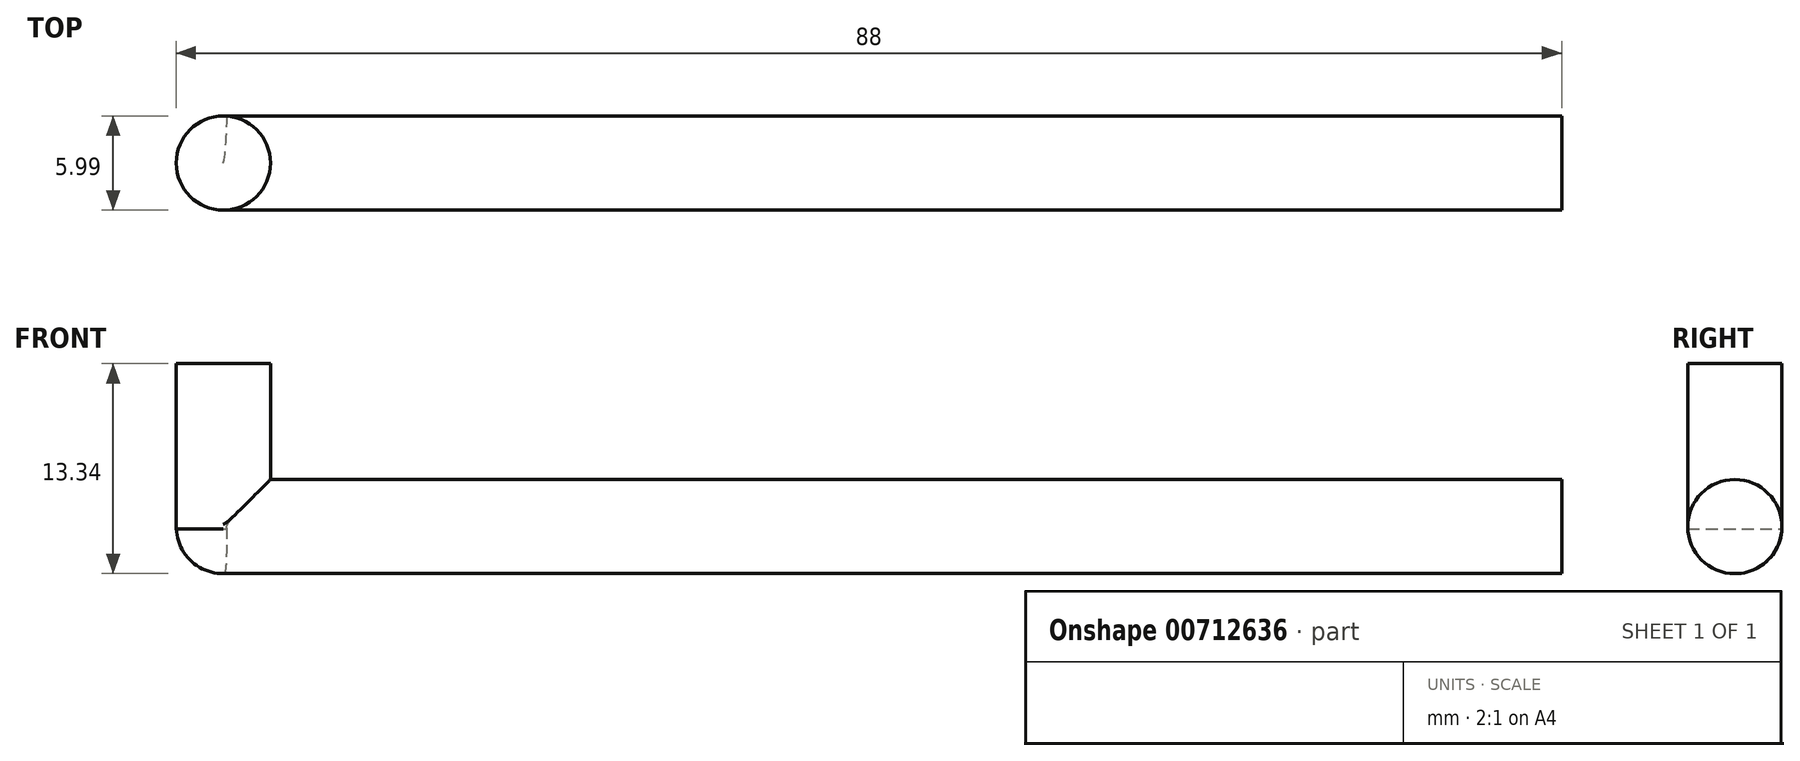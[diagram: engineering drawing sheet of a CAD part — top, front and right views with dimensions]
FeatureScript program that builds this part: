
annotation { "Feature Type Name" : "Feature", "Feature Type Description" : "" }
export const myFeature = defineFeature(function(context is Context, id is Id, definition is map)
    precondition{}
    {
        {
            var Q0;
            Q0=qCreatedBy(makeId("Top.planeOp"),FACE);
            var sketch = newSketch(context, id + "F0", { "sketchPlane" : qUnion([Q0])});
            skLineSegment(sketch, "E0", {"start": v(-19.14, -2.93) * mm, "end": v(65.86, -2.93) * mm});
            skLineSegment(sketch, "E1", {"start": v(65.86, -2.93) * mm, "end": v(65.86, -5.92) * mm});
            skLineSegment(sketch, "E2", {"start": v(65.86, -5.92) * mm, "end": v(-19.14, -5.92) * mm});
            skLineSegment(sketch, "E3", {"start": v(-19.14, -5.92) * mm, "end": v(-19.14, -2.93) * mm});
            skSolve(sketch);
        }
        {
            var Q0;
            Q0=makeQuery(id+"F0.imprint","IMPRINT",FACE,{"disambiguationData":[TD([[makeQuery(id+"F0.imprint","IMPRINT",EDGE,{"derivedFrom":sQuery(id+"F0.wireOp",EDGE,"E0")}),-1.0]])]});
            var Q1;
            Q1=sQuery(id+"F0.wireOp",EDGE,"E2");
            revolve(context, id + "F1", {"surfaceOperationType" : NewSurfaceOperationType.NEW, "entities" : qUnion([Q0]), "axis" : qUnion([Q1]), "revolveType" : RevolveType.FULL});
        }
        {
            var Q0;
            Q0=makeQuery(id+"F1.opRevolve","SWEPT_FACE",FACE,{"disambiguationData":[OSD([sQuery(id+"F0.wireOp",EDGE,"E3")])]});
            var sketch = newSketch(context, id + "F2", { "sketchPlane" : qUnion([Q0])});
            skLineSegment(sketch, "E4.bottom", {"start": v(5.91, -2.99) * mm, "end": v(8.9, -2.99) * mm});
            skLineSegment(sketch, "E4.top", {"start": v(5.91, 10.35) * mm, "end": v(8.9, 10.35) * mm});
            skLineSegment(sketch, "E4.left", {"start": v(5.91, -2.99) * mm, "end": v(5.91, 10.35) * mm});
            skLineSegment(sketch, "E4.right", {"start": v(8.9, -2.99) * mm, "end": v(8.9, 10.35) * mm});
            skLineSegment(sketch, "E5", {"start": v(2.93, 0) * mm, "end": v(5.92, 0) * mm});
            skSolve(sketch);
        }
        {
            var Q0;
            {var subQ0=sQuery(id+"F2.wireOp",EDGE,"E4.top");Q0=makeQuery(id+"F2.imprint","IMPRINT",FACE,{"disambiguationData":[TD([[makeQuery(id+"F2.imprint","IMPRINT",EDGE,{"derivedFrom":subQ0}),-1.0]])]});}
            var Q1;
            {var subQ1=makeQuery(id+"F1.opRevolve","SWEPT_EDGE",EDGE,{"disambiguationData":[OSD([sQuery(id+"F0.wireOp",EDGE,"E0"),sQuery(id+"F0.wireOp",EDGE,"E3")])]});var subQ4=sQuery(id+"F2.wireOp",EDGE,"E4.right");var subQ5=makeQuery(id+"F2.imprint","INTERSECT",VERTEX,{"disambiguationData":[OD(0.0)],"derivedFrom":[subQ1,subQ4]});Q1=makeQuery(id+"F2.imprint","IMPRINT",FACE,{"disambiguationData":[TD([[makeQuery(id+"F2.imprint","IMPRINT",EDGE,{"disambiguationData":[TD([[subQ5,-1.0]])],"derivedFrom":subQ4}),1.0]])]});}
            var Q2;
            Q2=sQuery(id+"F2.wireOp",EDGE,"E4.left");
            revolve(context, id + "F3", {"operationType" : NewBodyOperationType.ADD, "surfaceOperationType" : NewSurfaceOperationType.NEW, "entities" : qUnion([Q0, Q1]), "axis" : qUnion([Q2]), "revolveType" : RevolveType.FULL});
        }
    });
